# Revit family: OFFICE LV v2
name_source: partatom
category: Lighting Fixtures
units: mm (PartAtom-declared; Revit-internal decimal feet)

## family parameters
Cut with Voids When Loaded = No
Host = Face
Light Source = Yes
Maintain Annotation Orientation = Yes
Part Type = Normal
Room Calculation Point = No
Round Connector Dimension = Use Diameter
Shared = No

## types (30) — shared parameters
Color Filter = 16777215
Default Elevation = 1219 mm
Dimming Lamp Color Temperature Shift = <None>
Emit from Line Length = 610 mm
LuxLight_Alto = 73 mm  [stored 0.239501 ft]
LuxLight_Ancho = 46 mm  [stored 0.150919 ft]
Manufacturer = LUXLIGHT
Tilt Angle = -90.00°
zero-valued in all types: LuxLight_AltoAreaLuminosa, LuxLight_Amperios, LuxLight_Diametro, LuxLight_DiametroAreaLuminosa, LuxLight_ProtuberanciaTecho

## per-type parameters (varying)
| type | LuxLight_AnchoAreaLuminosa | LuxLight_Largo | LuxLight_LargoAreaLuminosa | LuxLight_Lumenes | LuxLight_Temperatura | LuxLight_Watios | Photometric Web File |
| LXLOFNLVx0293 | 35 mm | 560 mm | 500 mm | 1050 lm | 3000 K | 12 W | OFFICE LV LXLOFNLV20293 .ies |
| LXLOFNLVx0235 | 34 mm  [stored 0.111549 ft] | 560 mm | 560 mm | 1100 lm | 3500 K | 12 W | OFFICE LV LXLOFNLV20235.ies |
| LXLOFNLVx0294 | 34 mm  [stored 0.111549 ft] | 560 mm | 560 mm | 1154 lm | 4000 K | 12 W | OFFICE LV LXLOFNLV20294 .ies |
| LXLOFNLVx0393 | 34 mm  [stored 0.111549 ft] | 840 mm | 840 mm | 1575 lm | 3000 K | 18 W | OFFICE LV LXLOFNLV20393 .ies |
| LXLOFNLVx0335 | 34 mm  [stored 0.111549 ft] | 840 mm | 840 mm | 1650 lm | 3500 K | 18 W | OFFICE LV LXLOFNLV20335.ies |
| LXLOFNLVx0394 | 34 mm  [stored 0.111549 ft] | 840 mm | 840 mm | 1731 lm | 4000 K | 18 W | OFFICE LV LXLOFNLV20394 .ies |
| LXLOFNLVx0493 | 34 mm  [stored 0.111549 ft] | 1120 mm | 1120 mm | 2100 lm | 3000 K | 24 W | OFFICE LV LXLOFNLV20493 .ies |
| LXLOFNLVx0435 | 34 mm  [stored 0.111549 ft] | 1120 mm | 1120 mm | 2200 lm | 3500 K | 24 W | OFFICE LV LXLOFNLV20435.ies |
| LXLOFNLVx0494 | 34 mm  [stored 0.111549 ft] | 1120 mm | 1120 mm | 2308 lm | 4000 K | 24 W | OFFICE LV LXLOFNLV20494 .ies |
| LXLOFNLVx0593 | 34 mm  [stored 0.111549 ft] | 1400 mm | 1400 mm | 2625 lm | 3000 K | 30 W | OFFICE LV LXLOFNLV20593 .ies |
| LXLOFNLVx0535 | 34 mm  [stored 0.111549 ft] | 1400 mm | 1400 mm | 2750 lm | 3500 K | 30 W | OFFICE LV LXLOFNLV20535.ies |
| LXLOFNLVx0594 | 34 mm  [stored 0.111549 ft] | 1400 mm | 1400 mm | 2885 lm | 4000 K | 30 W | OFFICE LV LXLOFNLV20594 .ies |
| LXLOFNLVx0693 | 34 mm  [stored 0.111549 ft] | 1680 mm | 1680 mm | 3150 lm | 3000 K | 36 W | OFFICE LV LXLOFNLV20693.ies |
| LXLOFNLVx0635 | 34 mm  [stored 0.111549 ft] | 1680 mm | 1680 mm | 3300 lm | 3500 K | 36 W | OFFICE LV LXLOFNLV20635.ies |
| LXLOFNLVx0694 | 34 mm  [stored 0.111549 ft] | 1680 mm | 1680 mm | 3462 lm | 4000 K | 36 W | OFFICE LV LXLOFNLV20694 .ies |
| LXLOFNLVx0793 | 34 mm  [stored 0.111549 ft] | 1960 mm | 1960 mm | 3675 lm | 3000 K | 42 W | OFFICE LV LXLOFNLV20793 .ies |
| LXLOFNLVx0735 | 34 mm  [stored 0.111549 ft] | 1960 mm | 1960 mm | 3850 lm | 3500 K | 42 W | OFFICE LV LXLOFNLV20735.ies |
| LXLOFNLVx0794 | 34 mm  [stored 0.111549 ft] | 1960 mm | 1960 mm | 4039 lm | 4000 K | 42 W | OFFICE LV LXLOFNLV20794 .ies |
| LXLOFNLVx0893 | 34 mm  [stored 0.111549 ft] | 2240 mm | 2240 mm | 4200 lm | 3000 K | 48 W | OFFICE LV LXLOFNLV20893 .ies |
| LXLOFNLVx0835 | 34 mm  [stored 0.111549 ft] | 2240 mm | 2240 mm | 4400 lm | 3500 K | 48 W | OFFICE LV LXLOFNLV20835.ies |
| LXLOFNLVx0894 | 34 mm  [stored 0.111549 ft] | 2240 mm | 2240 mm | 4616 lm | 4000 K | 48 W | OFFICE LV LXLOFNLV20894 .ies |
| LXLOFNLVx0993 | 34 mm  [stored 0.111549 ft] | 2520 mm | 2520 mm | 4725 lm | 3000 K | 54 W | OFFICE LV LXLOFNLV20993 .ies |
| LXLOFNLVx0935 | 34 mm  [stored 0.111549 ft] | 2520 mm | 2520 mm | 4950 lm | 3500 K | 54 W | OFFICE LV LXLOFNLV20935.ies |
| LXLOFNLVx0994 | 34 mm  [stored 0.111549 ft] | 2520 mm | 2520 mm | 5193 lm | 4000 K | 54 W | OFFICE LV LXLOFNLV20994 .ies |
| LXLOFNLVx1093 | 34 mm  [stored 0.111549 ft] | 2800 mm | 2800 mm | 5250 lm | 3000 K | 60 W | OFFICE LV LXLOFNLV21093 .ies |
| LXLOFNLVx1035 | 34 mm  [stored 0.111549 ft] | 2800 mm | 2800 mm | 5500 lm | 3500 K | 60 W | OFFICE LV LXLOFNLV21035.ies |
| LXLOFNLVx1094 | 34 mm  [stored 0.111549 ft] | 2800 mm | 2800 mm | 5770 lm | 4000 K | 60 W | OFFICE LV LXLOFNLV21094 .ies |
| LXLOFNLVx1193 | 34 mm  [stored 0.111549 ft] | 3080 mm  [stored 10.105 ft] | 3080 mm  [stored 10.105 ft] | 5775 lm | 3000 K | 66 W | OFFICE LV LXLOFNLV21193 .ies |
| LXLOFNLVx1135 | 34 mm  [stored 0.111549 ft] | 3080 mm  [stored 10.105 ft] | 3080 mm  [stored 10.105 ft] | 6050 lm | 3500 K | 66 W | OFFICE LV LXLOFNLV21135.ies |
| LXLOFNLVx1194 | 34 mm  [stored 0.111549 ft] | 3080 mm  [stored 10.105 ft] | 3080 mm  [stored 10.105 ft] | 6347 lm | 4000 K | 66 W | OFFICE LV LXLOFNLV21194 .ies |

note: [stored X ft] marks values corroborated as IEEE doubles in the binary element streams (Revit-internal decimal feet)

## geometry (parser evidence)
native form markers: Sweep x3
no freeform markers — native parametric forms only
